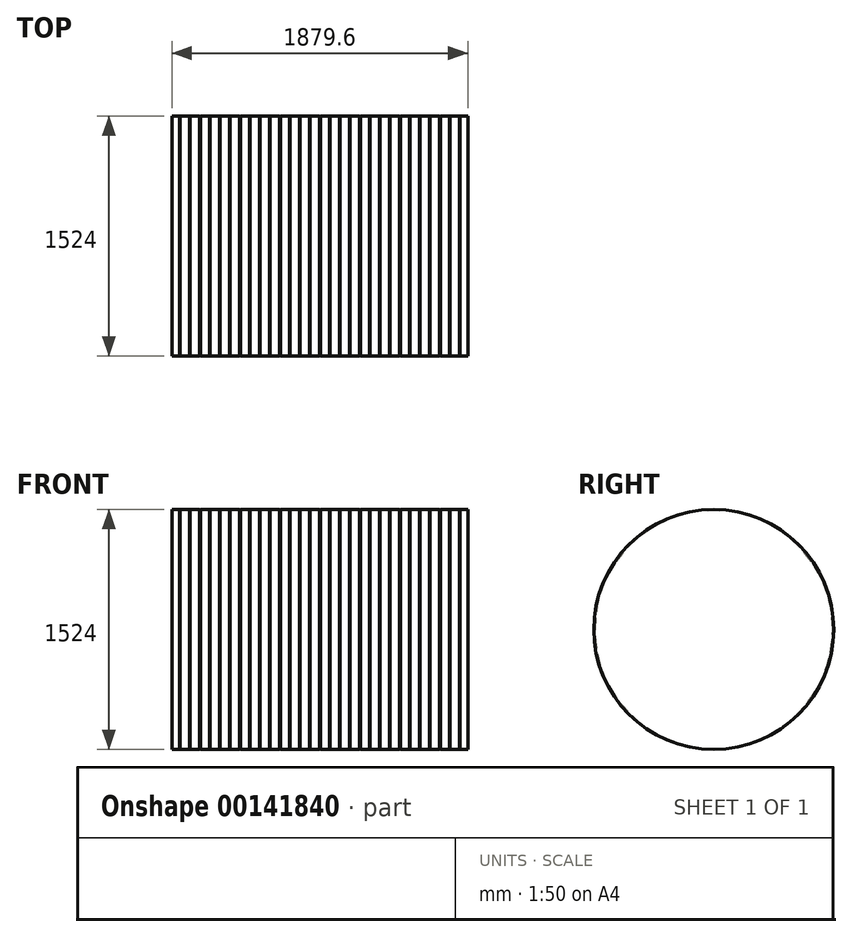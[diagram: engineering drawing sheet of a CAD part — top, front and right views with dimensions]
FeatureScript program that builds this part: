
annotation { "Feature Type Name" : "Feature", "Feature Type Description" : "" }
export const myFeature = defineFeature(function(context is Context, id is Id, definition is map)
    precondition{}
    {
        {
            var Q0;
            Q0=qCreatedBy(makeId("Front.planeOp"),FACE);
            var sketch = newSketch(context, id + "F0", { "sketchPlane" : qUnion([Q0])});
            skLineSegment(sketch, "E0", {"start": v(-939.8, 0) * mm, "end": v(939.8, 0) * mm, "construction": true});
            skLineSegment(sketch, "E1.0", {"start": v(-939.8, 762) * mm, "end": v(939.8, 762) * mm, "construction": true});
            skLineSegment(sketch, "E2", {"start": v(0, 0) * mm, "end": v(0, 1111.79) * mm, "construction": true});
            skLineSegment(sketch, "E3.0", {"start": v(-63.5, 0) * mm, "end": v(-63.5, 847.57) * mm, "construction": true});
            skLineSegment(sketch, "E4.0", {"start": v(-939.8, 755.65) * mm, "end": v(939.8, 755.65) * mm, "construction": true});
            skLineSegment(sketch, "E5.0", {"start": v(-939.8, 758.83) * mm, "end": v(939.8, 758.83) * mm, "construction": true});
            skLineSegment(sketch, "E6", {"start": v(0, 758.83) * mm, "end": v(-3.18, 758.83) * mm});
            skLineSegment(sketch, "E7", {"start": v(-3.18, 758.83) * mm, "end": v(-3.18, 762) * mm});
            skLineSegment(sketch, "E8", {"start": v(-63.5, 755.65) * mm, "end": v(-65, 755.65) * mm});
            skLineSegment(sketch, "E9", {"start": v(-65, 755.65) * mm, "end": v(-65, 762) * mm});
            skLineSegment(sketch, "E10.MirrorCS", {"start": v(-62, 755.65) * mm, "end": v(-62, 762) * mm});
            skLineSegment(sketch, "E11.MirrorCS", {"start": v(-63.5, 755.65) * mm, "end": v(-62, 755.65) * mm});
            skLineSegment(sketch, "E12.MirrorCS", {"start": v(-127, 0) * mm, "end": v(-127, 847.57) * mm, "construction": true});
            skLineSegment(sketch, "E13.MirrorCS", {"start": v(0, 758.83) * mm, "end": v(3.18, 758.83) * mm});
            skLineSegment(sketch, "E14.MirrorCS", {"start": v(3.18, 758.83) * mm, "end": v(3.18, 762) * mm});
            skLineSegment(sketch, "E15.1.0.0", {"start": v(-128.5, 755.65) * mm, "end": v(-128.5, 762) * mm});
            skLineSegment(sketch, "E15.1.0.1", {"start": v(-125.5, 755.65) * mm, "end": v(-125.5, 762) * mm});
            skLineSegment(sketch, "E15.1.0.2", {"start": v(-127, 755.65) * mm, "end": v(-128.5, 755.65) * mm});
            skLineSegment(sketch, "E15.1.0.3", {"start": v(-127, 755.65) * mm, "end": v(-125.5, 755.65) * mm});
            skLineSegment(sketch, "E15.2.0.0", {"start": v(-192, 755.65) * mm, "end": v(-192, 762) * mm});
            skLineSegment(sketch, "E15.2.0.1", {"start": v(-189, 755.65) * mm, "end": v(-189, 762) * mm});
            skLineSegment(sketch, "E15.2.0.2", {"start": v(-190.5, 755.65) * mm, "end": v(-192, 755.65) * mm});
            skLineSegment(sketch, "E15.2.0.3", {"start": v(-190.5, 755.65) * mm, "end": v(-189, 755.65) * mm});
            skLineSegment(sketch, "E15.4.0.0", {"start": v(-319, 755.65) * mm, "end": v(-319, 762) * mm});
            skLineSegment(sketch, "E15.4.0.1", {"start": v(-316, 755.65) * mm, "end": v(-316, 762) * mm});
            skLineSegment(sketch, "E15.4.0.2", {"start": v(-317.5, 755.65) * mm, "end": v(-319, 755.65) * mm});
            skLineSegment(sketch, "E15.4.0.3", {"start": v(-317.5, 755.65) * mm, "end": v(-316, 755.65) * mm});
            skLineSegment(sketch, "E15.5.0.0", {"start": v(-382.5, 755.65) * mm, "end": v(-382.5, 762) * mm});
            skLineSegment(sketch, "E15.5.0.1", {"start": v(-379.5, 755.65) * mm, "end": v(-379.5, 762) * mm});
            skLineSegment(sketch, "E15.5.0.2", {"start": v(-381, 755.65) * mm, "end": v(-382.5, 755.65) * mm});
            skLineSegment(sketch, "E15.5.0.3", {"start": v(-381, 755.65) * mm, "end": v(-379.5, 755.65) * mm});
            skLineSegment(sketch, "E15.6.0.0", {"start": v(-446, 755.65) * mm, "end": v(-446, 762) * mm});
            skLineSegment(sketch, "E15.6.0.1", {"start": v(-443, 755.65) * mm, "end": v(-443, 762) * mm});
            skLineSegment(sketch, "E15.6.0.2", {"start": v(-444.5, 755.65) * mm, "end": v(-446, 755.65) * mm});
            skLineSegment(sketch, "E15.6.0.3", {"start": v(-444.5, 755.65) * mm, "end": v(-443, 755.65) * mm});
            skLineSegment(sketch, "E15.8.0.0", {"start": v(-573, 755.65) * mm, "end": v(-573, 762) * mm});
            skLineSegment(sketch, "E15.8.0.1", {"start": v(-570, 755.65) * mm, "end": v(-570, 762) * mm});
            skLineSegment(sketch, "E15.8.0.2", {"start": v(-571.5, 755.65) * mm, "end": v(-573, 755.65) * mm});
            skLineSegment(sketch, "E15.8.0.3", {"start": v(-571.5, 755.65) * mm, "end": v(-570, 755.65) * mm});
            skLineSegment(sketch, "E15.9.0.0", {"start": v(-636.5, 755.65) * mm, "end": v(-636.5, 762) * mm});
            skLineSegment(sketch, "E15.9.0.1", {"start": v(-633.5, 755.65) * mm, "end": v(-633.5, 762) * mm});
            skLineSegment(sketch, "E15.9.0.2", {"start": v(-635, 755.65) * mm, "end": v(-636.5, 755.65) * mm});
            skLineSegment(sketch, "E15.9.0.3", {"start": v(-635, 755.65) * mm, "end": v(-633.5, 755.65) * mm});
            skLineSegment(sketch, "E15.10.0.0", {"start": v(-700, 755.65) * mm, "end": v(-700, 762) * mm});
            skLineSegment(sketch, "E15.10.0.1", {"start": v(-697, 755.65) * mm, "end": v(-697, 762) * mm});
            skLineSegment(sketch, "E15.10.0.2", {"start": v(-698.5, 755.65) * mm, "end": v(-700, 755.65) * mm});
            skLineSegment(sketch, "E15.10.0.3", {"start": v(-698.5, 755.65) * mm, "end": v(-697, 755.65) * mm});
            skLineSegment(sketch, "E15.direction1", {"start": v(-65, 755.65) * mm, "end": v(-128.5, 755.65) * mm, "construction": true});
            skLineSegment(sketch, "E16.1.0.0", {"start": v(-827, 755.65) * mm, "end": v(-827, 762) * mm});
            skLineSegment(sketch, "E16.1.0.1", {"start": v(-824, 755.65) * mm, "end": v(-824, 762) * mm});
            skLineSegment(sketch, "E16.1.0.2", {"start": v(-825.5, 755.65) * mm, "end": v(-827, 755.65) * mm});
            skLineSegment(sketch, "E16.1.0.3", {"start": v(-825.5, 755.65) * mm, "end": v(-824, 755.65) * mm});
            skLineSegment(sketch, "E16.2.0.0", {"start": v(-890.5, 755.65) * mm, "end": v(-890.5, 762) * mm});
            skLineSegment(sketch, "E16.2.0.1", {"start": v(-887.5, 755.65) * mm, "end": v(-887.5, 762) * mm});
            skLineSegment(sketch, "E16.2.0.2", {"start": v(-889, 755.65) * mm, "end": v(-890.5, 755.65) * mm});
            skLineSegment(sketch, "E16.2.0.3", {"start": v(-889, 755.65) * mm, "end": v(-887.5, 755.65) * mm});
            skLineSegment(sketch, "E16.direction1", {"start": v(-763.5, 755.65) * mm, "end": v(-827, 755.65) * mm, "construction": true});
            skLineSegment(sketch, "E17.MirrorCS", {"start": v(825.5, 755.65) * mm, "end": v(827, 755.65) * mm});
            skLineSegment(sketch, "E18.MirrorCS", {"start": v(827, 755.65) * mm, "end": v(827, 762) * mm});
            skLineSegment(sketch, "E19.MirrorCS", {"start": v(190.5, 755.65) * mm, "end": v(192, 755.65) * mm});
            skLineSegment(sketch, "E20.MirrorCS", {"start": v(825.5, 755.65) * mm, "end": v(824, 755.65) * mm});
            skLineSegment(sketch, "E21.MirrorCS", {"start": v(381, 755.65) * mm, "end": v(382.5, 755.65) * mm});
            skLineSegment(sketch, "E22.MirrorCS", {"start": v(824, 755.65) * mm, "end": v(824, 762) * mm});
            skLineSegment(sketch, "E23.MirrorCS", {"start": v(379.5, 755.65) * mm, "end": v(379.5, 762) * mm});
            skLineSegment(sketch, "E24.MirrorCS", {"start": v(633.5, 755.65) * mm, "end": v(633.5, 762) * mm});
            skLineSegment(sketch, "E25.MirrorCS", {"start": v(444.5, 755.65) * mm, "end": v(446, 755.65) * mm});
            skLineSegment(sketch, "E26.MirrorCS", {"start": v(190.5, 755.65) * mm, "end": v(189, 755.65) * mm});
            skLineSegment(sketch, "E27.MirrorCS", {"start": v(443, 755.65) * mm, "end": v(443, 762) * mm});
            skLineSegment(sketch, "E28.MirrorCS", {"start": v(381, 755.65) * mm, "end": v(379.5, 755.65) * mm});
            skLineSegment(sketch, "E29.MirrorCS", {"start": v(635, 755.65) * mm, "end": v(636.5, 755.65) * mm});
            skLineSegment(sketch, "E30.MirrorCS", {"start": v(444.5, 755.65) * mm, "end": v(443, 755.65) * mm});
            skLineSegment(sketch, "E31.MirrorCS", {"start": v(382.5, 755.65) * mm, "end": v(382.5, 762) * mm});
            skLineSegment(sketch, "E32.MirrorCS", {"start": v(636.5, 755.65) * mm, "end": v(636.5, 762) * mm});
            skLineSegment(sketch, "E33.MirrorCS", {"start": v(635, 755.65) * mm, "end": v(633.5, 755.65) * mm});
            skLineSegment(sketch, "E34.MirrorCS", {"start": v(63.5, 755.65) * mm, "end": v(65, 755.65) * mm});
            skLineSegment(sketch, "E35.MirrorCS", {"start": v(189, 755.65) * mm, "end": v(189, 762) * mm});
            skLineSegment(sketch, "E36.MirrorCS", {"start": v(446, 755.65) * mm, "end": v(446, 762) * mm});
            skLineSegment(sketch, "E37.MirrorCS", {"start": v(192, 755.65) * mm, "end": v(192, 762) * mm});
            skLineSegment(sketch, "E38.MirrorCS", {"start": v(698.5, 755.65) * mm, "end": v(700, 755.65) * mm});
            skLineSegment(sketch, "E39.MirrorCS", {"start": v(65, 755.65) * mm, "end": v(65, 762) * mm});
            skLineSegment(sketch, "E40.MirrorCS", {"start": v(62, 755.65) * mm, "end": v(62, 762) * mm});
            skLineSegment(sketch, "E41.MirrorCS", {"start": v(63.5, 755.65) * mm, "end": v(62, 755.65) * mm});
            skLineSegment(sketch, "E42.MirrorCS", {"start": v(570, 755.65) * mm, "end": v(570, 762) * mm});
            skLineSegment(sketch, "E43.MirrorCS", {"start": v(316, 755.65) * mm, "end": v(316, 762) * mm});
            skLineSegment(sketch, "E44.MirrorCS", {"start": v(571.5, 755.65) * mm, "end": v(570, 755.65) * mm});
            skLineSegment(sketch, "E45.MirrorCS", {"start": v(127, 755.65) * mm, "end": v(128.5, 755.65) * mm});
            skLineSegment(sketch, "E46.MirrorCS", {"start": v(317.5, 755.65) * mm, "end": v(316, 755.65) * mm});
            skLineSegment(sketch, "E47.MirrorCS", {"start": v(317.5, 755.65) * mm, "end": v(319, 755.65) * mm});
            skLineSegment(sketch, "E48.MirrorCS", {"start": v(698.5, 755.65) * mm, "end": v(697, 755.65) * mm});
            skLineSegment(sketch, "E49.MirrorCS", {"start": v(890.5, 755.65) * mm, "end": v(890.5, 762) * mm});
            skLineSegment(sketch, "E50.MirrorCS", {"start": v(887.5, 755.65) * mm, "end": v(887.5, 762) * mm});
            skLineSegment(sketch, "E51.MirrorCS", {"start": v(125.5, 755.65) * mm, "end": v(125.5, 762) * mm});
            skLineSegment(sketch, "E52.MirrorCS", {"start": v(571.5, 755.65) * mm, "end": v(573, 755.65) * mm});
            skLineSegment(sketch, "E53.MirrorCS", {"start": v(697, 755.65) * mm, "end": v(697, 762) * mm});
            skLineSegment(sketch, "E54.MirrorCS", {"start": v(128.5, 755.65) * mm, "end": v(128.5, 762) * mm});
            skLineSegment(sketch, "E55.MirrorCS", {"start": v(889, 755.65) * mm, "end": v(890.5, 755.65) * mm});
            skLineSegment(sketch, "E56.MirrorCS", {"start": v(127, 755.65) * mm, "end": v(125.5, 755.65) * mm});
            skLineSegment(sketch, "E57.MirrorCS", {"start": v(319, 755.65) * mm, "end": v(319, 762) * mm});
            skLineSegment(sketch, "E58.MirrorCS", {"start": v(573, 755.65) * mm, "end": v(573, 762) * mm});
            skLineSegment(sketch, "E59.MirrorCS", {"start": v(700, 755.65) * mm, "end": v(700, 762) * mm});
            skLineSegment(sketch, "E60.MirrorCS", {"start": v(889, 755.65) * mm, "end": v(887.5, 755.65) * mm});
            skLineSegment(sketch, "E61.MirrorCS", {"start": v(763.5, 755.65) * mm, "end": v(827, 755.65) * mm, "construction": true});
            skLineSegment(sketch, "E62.MirrorCS", {"start": v(65, 755.65) * mm, "end": v(128.5, 755.65) * mm, "construction": true});
            skLineSegment(sketch, "E63.1.0.0", {"start": v(-190.5, 0) * mm, "end": v(-190.5, 847.57) * mm, "construction": true});
            skLineSegment(sketch, "E63.2.0.0", {"start": v(-254, 0) * mm, "end": v(-254, 847.57) * mm, "construction": true});
            skLineSegment(sketch, "E63.3.0.0", {"start": v(-317.5, 0) * mm, "end": v(-317.5, 847.57) * mm, "construction": true});
            skLineSegment(sketch, "E63.4.0.0", {"start": v(-381, 0) * mm, "end": v(-381, 847.57) * mm, "construction": true});
            skLineSegment(sketch, "E63.5.0.0", {"start": v(-444.5, 0) * mm, "end": v(-444.5, 847.57) * mm, "construction": true});
            skLineSegment(sketch, "E63.6.0.0", {"start": v(-508, 0) * mm, "end": v(-508, 847.57) * mm, "construction": true});
            skLineSegment(sketch, "E63.10.0.0", {"start": v(-762, 0) * mm, "end": v(-762, 847.57) * mm, "construction": true});
            skLineSegment(sketch, "E63.11.0.0", {"start": v(-825.5, 0) * mm, "end": v(-825.5, 847.57) * mm, "construction": true});
            skLineSegment(sketch, "E63.direction1", {"start": v(-127, 0) * mm, "end": v(-190.5, 0) * mm, "construction": true});
            skLineSegment(sketch, "E64.1.0.0", {"start": v(-254, 758.83) * mm, "end": v(-250.83, 758.83) * mm});
            skLineSegment(sketch, "E64.1.0.1", {"start": v(-250.83, 758.83) * mm, "end": v(-250.83, 762) * mm});
            skLineSegment(sketch, "E64.1.0.2", {"start": v(-254, 758.83) * mm, "end": v(-257.18, 758.83) * mm});
            skLineSegment(sketch, "E64.1.0.3", {"start": v(-257.18, 758.83) * mm, "end": v(-257.18, 762) * mm});
            skLineSegment(sketch, "E64.2.0.0", {"start": v(-508, 758.83) * mm, "end": v(-504.83, 758.83) * mm});
            skLineSegment(sketch, "E64.2.0.1", {"start": v(-504.82, 758.83) * mm, "end": v(-504.82, 762) * mm});
            skLineSegment(sketch, "E64.2.0.2", {"start": v(-508, 758.83) * mm, "end": v(-511.17, 758.83) * mm});
            skLineSegment(sketch, "E64.2.0.3", {"start": v(-511.18, 758.83) * mm, "end": v(-511.18, 762) * mm});
            skLineSegment(sketch, "E64.3.0.0", {"start": v(-762, 758.83) * mm, "end": v(-758.83, 758.83) * mm});
            skLineSegment(sketch, "E64.3.0.1", {"start": v(-758.82, 758.83) * mm, "end": v(-758.82, 762) * mm});
            skLineSegment(sketch, "E64.3.0.2", {"start": v(-762, 758.83) * mm, "end": v(-765.17, 758.83) * mm});
            skLineSegment(sketch, "E64.3.0.3", {"start": v(-765.18, 758.83) * mm, "end": v(-765.18, 762) * mm});
            skLineSegment(sketch, "E64.direction1", {"start": v(-3.18, 758.83) * mm, "end": v(-257.18, 758.83) * mm, "construction": true});
            skPoint(sketch, "E65.orphan", {"position": v(0, 847.57) * mm});
            skLineSegment(sketch, "E66.MirrorCS", {"start": v(254, 758.83) * mm, "end": v(250.83, 758.83) * mm});
            skLineSegment(sketch, "E67.MirrorCS", {"start": v(257.18, 758.83) * mm, "end": v(257.18, 762) * mm});
            skLineSegment(sketch, "E68.MirrorCS", {"start": v(254, 758.83) * mm, "end": v(257.18, 758.83) * mm});
            skLineSegment(sketch, "E69.MirrorCS", {"start": v(250.83, 758.83) * mm, "end": v(250.83, 762) * mm});
            skLineSegment(sketch, "E70.MirrorCS", {"start": v(511.18, 758.83) * mm, "end": v(511.18, 762) * mm});
            skLineSegment(sketch, "E71.MirrorCS", {"start": v(504.82, 758.83) * mm, "end": v(504.82, 762) * mm});
            skLineSegment(sketch, "E72.MirrorCS", {"start": v(508, 758.83) * mm, "end": v(504.83, 758.83) * mm});
            skLineSegment(sketch, "E73.MirrorCS", {"start": v(508, 758.83) * mm, "end": v(511.17, 758.83) * mm});
            skLineSegment(sketch, "E74.MirrorCS", {"start": v(765.18, 758.83) * mm, "end": v(765.18, 762) * mm});
            skLineSegment(sketch, "E75.MirrorCS", {"start": v(762, 758.83) * mm, "end": v(758.83, 758.83) * mm});
            skLineSegment(sketch, "E76.MirrorCS", {"start": v(762, 758.83) * mm, "end": v(765.17, 758.83) * mm});
            skLineSegment(sketch, "E77.MirrorCS", {"start": v(758.82, 758.83) * mm, "end": v(758.82, 762) * mm});
            skLineSegment(sketch, "E78", {"start": v(3.18, 762) * mm, "end": v(62, 762) * mm});
            skLineSegment(sketch, "E79", {"start": v(65, 762) * mm, "end": v(125.5, 762) * mm});
            skLineSegment(sketch, "E80", {"start": v(128.5, 762) * mm, "end": v(189, 762) * mm});
            skLineSegment(sketch, "E81", {"start": v(192, 762) * mm, "end": v(250.83, 762) * mm});
            skLineSegment(sketch, "E82", {"start": v(257.18, 762) * mm, "end": v(316, 762) * mm});
            skLineSegment(sketch, "E83", {"start": v(319, 762) * mm, "end": v(379.5, 762) * mm});
            skLineSegment(sketch, "E84", {"start": v(382.5, 762) * mm, "end": v(443, 762) * mm});
            skLineSegment(sketch, "E85", {"start": v(446, 762) * mm, "end": v(504.82, 762) * mm});
            skLineSegment(sketch, "E86", {"start": v(511.18, 762) * mm, "end": v(570, 762) * mm});
            skLineSegment(sketch, "E87", {"start": v(573, 762) * mm, "end": v(633.5, 762) * mm});
            skLineSegment(sketch, "E88", {"start": v(636.5, 762) * mm, "end": v(697, 762) * mm});
            skLineSegment(sketch, "E89", {"start": v(700, 762) * mm, "end": v(758.82, 762) * mm});
            skLineSegment(sketch, "E90", {"start": v(765.18, 762) * mm, "end": v(824, 762) * mm});
            skLineSegment(sketch, "E91", {"start": v(827, 762) * mm, "end": v(887.5, 762) * mm});
            skLineSegment(sketch, "E92", {"start": v(890.5, 762) * mm, "end": v(939.8, 762) * mm});
            skLineSegment(sketch, "E93", {"start": v(939.8, 762) * mm, "end": v(939.8, 0) * mm});
            skLineSegment(sketch, "E94", {"start": v(-939.8, 0) * mm, "end": v(-939.8, 755.65) * mm});
            skLineSegment(sketch, "E95", {"start": v(-939.8, 755.65) * mm, "end": v(-939.8, 762) * mm});
            skLineSegment(sketch, "E96", {"start": v(-939.8, 762) * mm, "end": v(-890.5, 762) * mm});
            skLineSegment(sketch, "E97", {"start": v(-887.5, 762) * mm, "end": v(-827, 762) * mm});
            skLineSegment(sketch, "E98", {"start": v(-824, 762) * mm, "end": v(-765.18, 762) * mm});
            skLineSegment(sketch, "E99", {"start": v(-785.3, 722.1) * mm, "end": v(-780.35, 722.1) * mm});
            skLineSegment(sketch, "E100", {"start": v(-758.82, 762) * mm, "end": v(-700, 762) * mm});
            skLineSegment(sketch, "E101", {"start": v(-697, 762) * mm, "end": v(-636.5, 762) * mm});
            skLineSegment(sketch, "E102", {"start": v(-633.5, 762) * mm, "end": v(-573, 762) * mm});
            skLineSegment(sketch, "E103", {"start": v(-570, 762) * mm, "end": v(-511.18, 762) * mm});
            skLineSegment(sketch, "E104", {"start": v(-504.82, 762) * mm, "end": v(-446, 762) * mm});
            skLineSegment(sketch, "E105", {"start": v(-443, 762) * mm, "end": v(-382.5, 762) * mm});
            skLineSegment(sketch, "E106", {"start": v(-379.5, 762) * mm, "end": v(-319, 762) * mm});
            skLineSegment(sketch, "E107", {"start": v(-316, 762) * mm, "end": v(-257.18, 762) * mm});
            skLineSegment(sketch, "E108", {"start": v(-250.83, 762) * mm, "end": v(-192, 762) * mm});
            skLineSegment(sketch, "E109", {"start": v(-189, 762) * mm, "end": v(-128.5, 762) * mm});
            skLineSegment(sketch, "E110", {"start": v(-125.5, 762) * mm, "end": v(-65, 762) * mm});
            skLineSegment(sketch, "E111", {"start": v(-62, 762) * mm, "end": v(-3.18, 762) * mm});
            skLineSegment(sketch, "E112", {"start": v(-939.8, 0) * mm, "end": v(939.8, 0) * mm});
            skSolve(sketch);
        }
        {
            var Q0;
            Q0=makeQuery(id+"F0.imprint","IMPRINT",FACE,{"disambiguationData":[TD([[makeQuery(id+"F0.imprint","IMPRINT",EDGE,{"derivedFrom":sQuery(id+"F0.wireOp",EDGE,"E6")}),1.0]])]});
            var Q1;
            Q1=sQuery(id+"F0.wireOp",EDGE,"E112");
            revolve(context, id + "F1", {"entities" : qUnion([Q0]), "axis" : qUnion([Q1]), "revolveType" : RevolveType.FULL});
        }
    });
